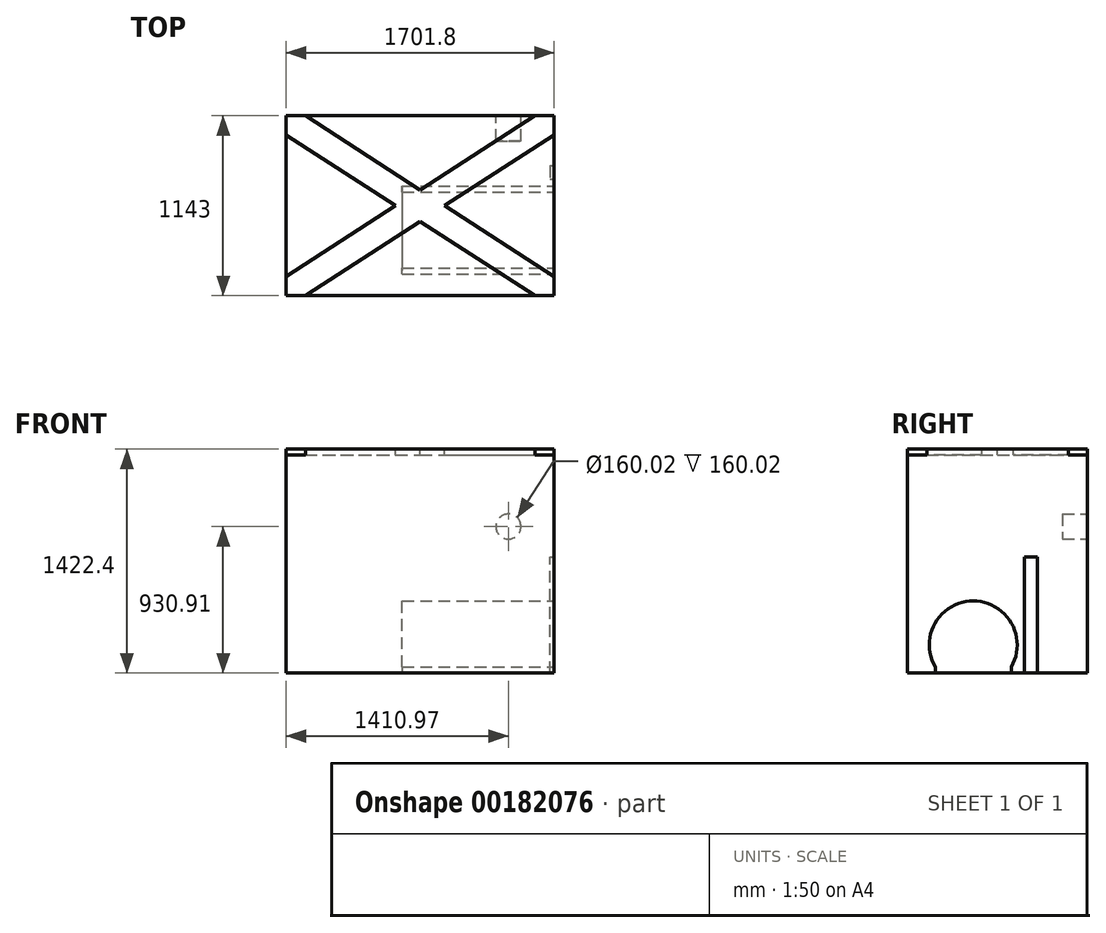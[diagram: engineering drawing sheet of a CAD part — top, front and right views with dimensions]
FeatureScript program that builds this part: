
annotation { "Feature Type Name" : "Feature", "Feature Type Description" : "" }
export const myFeature = defineFeature(function(context is Context, id is Id, definition is map)
    precondition{}
    {
        {
            var Q0;
            Q0=qCreatedBy(makeId("Top.planeOp"),FACE);
            var sketch = newSketch(context, id + "F0", { "sketchPlane" : qUnion([Q0])});
            skLineSegment(sketch, "E0.bottom", {"start": v(-857.3, 499.51) * mm, "end": v(844.5, 499.51) * mm});
            skLineSegment(sketch, "E0.top", {"start": v(-857.3, -643.49) * mm, "end": v(844.5, -643.49) * mm});
            skLineSegment(sketch, "E0.left", {"start": v(-857.3, 499.51) * mm, "end": v(-857.3, -643.49) * mm});
            skLineSegment(sketch, "E0.right", {"start": v(844.5, 499.51) * mm, "end": v(844.5, -643.49) * mm});
            skSolve(sketch);
        }
        {
            var Q0;
            Q0 = qSketchRegion(id + "F0", true);
            extrude(context, id + "F1", {"entities" : qUnion([Q0]), "depth" : 1422.4 * mm});
        }
        {
            var Q0;
            Q0=makeQuery(id+"F1.opExtrude","SWEPT_FACE",FACE,{"disambiguationData":[OSD([sQuery(id+"F0.wireOp",EDGE,"E0.bottom")])]});
            var sketch = newSketch(context, id + "F2", { "sketchPlane" : qUnion([Q0])});
            skCircle(sketch, "E1", {"center": v(-553.68, 930.91) * mm, "radius": 80.01 * mm});
            skSolve(sketch);
        }
        {
            var Q0;
            Q0 = qSketchRegion(id + "F2", true);
            extrude(context, id + "F3", {"entities" : qUnion([Q0]), "operationType" : NewBodyOperationType.REMOVE, "oppositeDirection" : true, "depth" : 160.02 * mm});
        }
        {
            var Q0;
            Q0=makeQuery(id+"F1.opExtrude","CAP_FACE",FACE,{"disambiguationData":[OSD([sQuery(id+"F0.wireOp",EDGE,"E0.bottom"),sQuery(id+"F0.wireOp",EDGE,"E0.top"),sQuery(id+"F0.wireOp",EDGE,"E0.left"),sQuery(id+"F0.wireOp",EDGE,"E0.right")])],"isStart":false});
            var sketch = newSketch(context, id + "F4", { "sketchPlane" : qUnion([Q0])});
            skLineSegment(sketch, "E2", {"start": v(-735.37, -643.49) * mm, "end": v(-6.4, -172.35) * mm});
            skLineSegment(sketch, "E3", {"start": v(-857.3, -521.57) * mm, "end": v(-161.67, -71.99) * mm});
            skLineSegment(sketch, "E4", {"start": v(722.59, 499.51) * mm, "end": v(844.5, 499.51) * mm});
            skLineSegment(sketch, "E5.trimOffspring", {"start": v(-6.4, 28.37) * mm, "end": v(722.59, 499.51) * mm});
            skLineSegment(sketch, "E6.trimOffspring", {"start": v(148.9, -71.99) * mm, "end": v(844.5, 377.6) * mm});
            skLineSegment(sketch, "E7", {"start": v(-857.3, 377.6) * mm, "end": v(-161.67, -71.99) * mm});
            skLineSegment(sketch, "E8", {"start": v(-735.37, 499.51) * mm, "end": v(-6.4, 28.37) * mm});
            skLineSegment(sketch, "E9.trimOffspring", {"start": v(148.9, -71.99) * mm, "end": v(844.5, -521.57) * mm});
            skLineSegment(sketch, "E10.trimOffspring", {"start": v(-6.4, -172.35) * mm, "end": v(722.59, -643.49) * mm});
            skSolve(sketch);
        }
        {
            var Q0;
            {var subQ10=sQuery(id+"F4.wireOp",EDGE,"E2");Q0=makeQuery(id+"F4.imprint","IMPRINT",FACE,{"disambiguationData":[TD([[makeQuery(id+"F4.imprint","IMPRINT",EDGE,{"derivedFrom":subQ10}),1.0]])]});}
            extrude(context, id + "F5", {"entities" : qUnion([Q0]), "operationType" : NewBodyOperationType.REMOVE, "oppositeDirection" : true, "depth" : 38.1 * mm});
        }
        {
            var Q0;
            Q0=makeQuery(id+"F1.opExtrude","SWEPT_FACE",FACE,{"disambiguationData":[OSD([sQuery(id+"F0.wireOp",EDGE,"E0.right")])]});
            var sketch = newSketch(context, id + "F6", { "sketchPlane" : qUnion([Q0])});
            skLineSegment(sketch, "E11", {"start": v(182.01, 0) * mm, "end": v(182.01, 736.6) * mm});
            skLineSegment(sketch, "E12", {"start": v(182.01, 736.6) * mm, "end": v(98.2, 736.6) * mm});
            skLineSegment(sketch, "E13", {"start": v(98.2, 0) * mm, "end": v(98.2, 736.6) * mm});
            skSolve(sketch);
        }
        {
            var Q0;
            {var subQ0=sQuery(id+"F6.wireOp",EDGE,"E11");Q0=makeQuery(id+"F6.imprint","IMPRINT",FACE,{"disambiguationData":[TD([[makeQuery(id+"F6.imprint","IMPRINT",EDGE,{"derivedFrom":subQ0}),1.0]])]});}
            extrude(context, id + "F7", {"entities" : qUnion([Q0]), "operationType" : NewBodyOperationType.REMOVE, "oppositeDirection" : true, "depth" : 25.4 * mm});
        }
        {
            var Q0;
            Q0=makeQuery(id+"F1.opExtrude","SWEPT_FACE",FACE,{"disambiguationData":[OSD([sQuery(id+"F0.wireOp",EDGE,"E0.right")])]});
            var sketch = newSketch(context, id + "F8", { "sketchPlane" : qUnion([Q0])});
            skLineSegment(sketch, "E14", {"start": v(14.37, 38.1) * mm, "end": v(14.37, 0) * mm});
            skLineSegment(sketch, "E15", {"start": v(-468.23, 38.1) * mm, "end": v(-468.23, 0) * mm});
            skArc(sketch, "E16", {"start": v(14.37, 38.1) * mm, "mid": v(-226.93, 458.35) * mm, "end": v(-468.23, 38.1) * mm});
            skPoint(sketch, "E16.third.point", {"position": v(-267.23, 455.43) * mm});
            skSolve(sketch);
        }
        {
            var Q0;
            {var subQ0=sQuery(id+"F8.wireOp",EDGE,"E14");Q0=makeQuery(id+"F8.imprint","IMPRINT",FACE,{"disambiguationData":[TD([[makeQuery(id+"F8.imprint","IMPRINT",EDGE,{"derivedFrom":subQ0}),-1.0]])]});}
            extrude(context, id + "F9", {"entities" : qUnion([Q0]), "operationType" : NewBodyOperationType.REMOVE, "oppositeDirection" : true, "depth" : 965.2 * mm});
        }
    });
